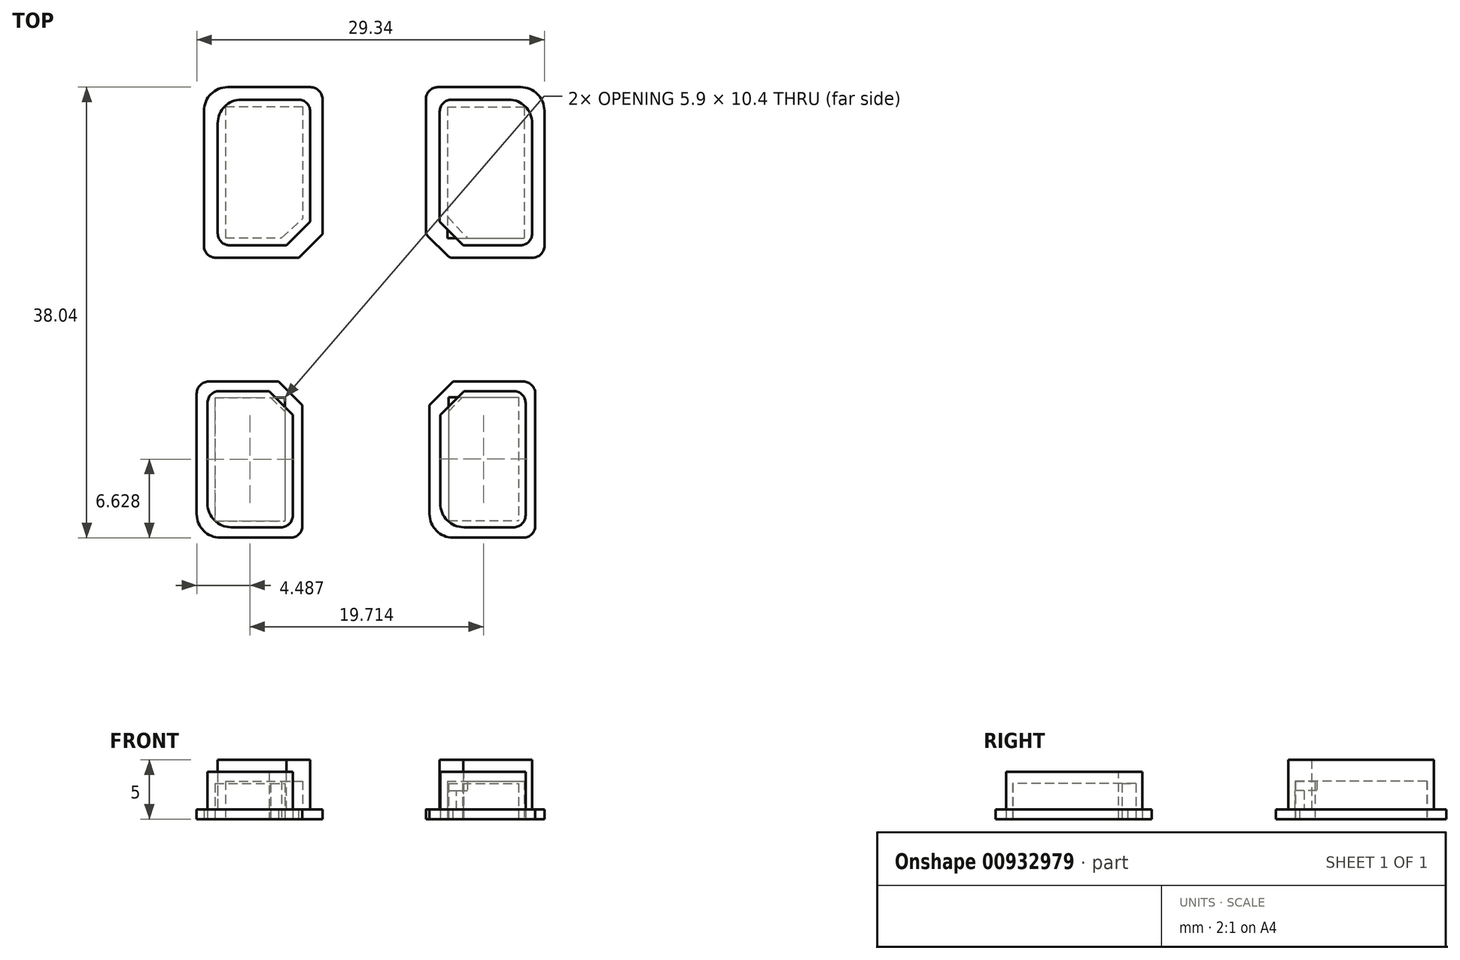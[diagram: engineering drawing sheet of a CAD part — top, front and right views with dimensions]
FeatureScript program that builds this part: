
annotation { "Feature Type Name" : "Feature", "Feature Type Description" : "" }
export const myFeature = defineFeature(function(context is Context, id is Id, definition is map)
    precondition{}
    {
        {
            var Q0;
            Q0=qCreatedBy(makeId("Top.planeOp"),FACE);
            var sketch = newSketch(context, id + "F0", { "sketchPlane" : qUnion([Q0])});
            skLineSegment(sketch, "E0.bottom", {"start": v(-38.74, 12.3) * mm, "end": v(-30.94, 12.3) * mm});
            skLineSegment(sketch, "E0.top", {"start": v(-38.74, 0) * mm, "end": v(-30.94, 0) * mm});
            skLineSegment(sketch, "E0.left", {"start": v(-38.74, 12.3) * mm, "end": v(-38.74, 0) * mm});
            skLineSegment(sketch, "E0.right", {"start": v(-30.94, 12.3) * mm, "end": v(-30.94, 0) * mm});
            skLineSegment(sketch, "E1.bottom", {"start": v(-39.9, 13.35) * mm, "end": v(-29.9, 13.35) * mm});
            skLineSegment(sketch, "E1.top", {"start": v(-39.9, -1.05) * mm, "end": v(-29.9, -1.05) * mm});
            skLineSegment(sketch, "E1.left", {"start": v(-39.9, 13.35) * mm, "end": v(-39.9, -1.05) * mm});
            skLineSegment(sketch, "E1.right", {"start": v(-29.9, 13.35) * mm, "end": v(-29.9, -1.05) * mm});
            skLineSegment(sketch, "E2.bottom", {"start": v(-20, 12.3) * mm, "end": v(-12.2, 12.3) * mm});
            skLineSegment(sketch, "E2.top", {"start": v(-20, 0) * mm, "end": v(-12.2, 0) * mm});
            skLineSegment(sketch, "E2.left", {"start": v(-20, 12.3) * mm, "end": v(-20, 0) * mm});
            skLineSegment(sketch, "E2.right", {"start": v(-12.2, 12.3) * mm, "end": v(-12.2, 0) * mm});
            skLineSegment(sketch, "E3.bottom", {"start": v(-21.17, 13.35) * mm, "end": v(-11.17, 13.35) * mm});
            skLineSegment(sketch, "E3.top", {"start": v(-21.17, -1.05) * mm, "end": v(-11.17, -1.05) * mm});
            skLineSegment(sketch, "E3.left", {"start": v(-21.17, 13.35) * mm, "end": v(-21.17, -1.05) * mm});
            skLineSegment(sketch, "E3.right", {"start": v(-11.17, 13.35) * mm, "end": v(-11.17, -1.05) * mm});
            skLineSegment(sketch, "E4.bottom", {"start": v(-38.08, 11.72) * mm, "end": v(-31.58, 11.72) * mm});
            skLineSegment(sketch, "E4.top", {"start": v(-38.08, 0.62) * mm, "end": v(-31.58, 0.62) * mm});
            skLineSegment(sketch, "E4.left", {"start": v(-38.08, 11.72) * mm, "end": v(-38.08, 0.62) * mm});
            skLineSegment(sketch, "E4.right", {"start": v(-31.58, 11.72) * mm, "end": v(-31.58, 0.62) * mm});
            skLineSegment(sketch, "E5.bottom", {"start": v(-19.36, 11.7) * mm, "end": v(-12.86, 11.7) * mm});
            skLineSegment(sketch, "E5.top", {"start": v(-19.36, 0.6) * mm, "end": v(-12.86, 0.6) * mm});
            skLineSegment(sketch, "E5.left", {"start": v(-19.36, 11.7) * mm, "end": v(-19.36, 0.6) * mm});
            skLineSegment(sketch, "E5.right", {"start": v(-12.86, 11.7) * mm, "end": v(-12.86, 0.6) * mm});
            skLineSegment(sketch, "E6", {"start": v(-33.34, 0.62) * mm, "end": v(-31.58, 2.25) * mm});
            skLineSegment(sketch, "E7", {"start": v(-19.36, 2.44) * mm, "end": v(-17.65, 0.6) * mm});
            skSolve(sketch);
        }
        {
            var Q0;
            Q0=makeQuery(id+"F0.imprint","IMPRINT",FACE,{"disambiguationData":[TD([[makeQuery(id+"F0.imprint","IMPRINT",EDGE,{"derivedFrom":sQuery(id+"F0.wireOp",EDGE,"E0.bottom")}),-1.0]])]});
            var Q1;
            Q1=makeQuery(id+"F0.imprint","IMPRINT",FACE,{"disambiguationData":[TD([[makeQuery(id+"F0.imprint","IMPRINT",EDGE,{"derivedFrom":sQuery(id+"F0.wireOp",EDGE,"E2.bottom")}),-1.0]])]});
            var Q2;
            Q2=makeQuery(id+"F0.imprint","IMPRINT",FACE,{"disambiguationData":[TD([[makeQuery(id+"F0.imprint","IMPRINT",EDGE,{"derivedFrom":sQuery(id+"F0.wireOp",EDGE,"E5.bottom")}),-1.0]])]});
            var Q3;
            Q3=makeQuery(id+"F0.imprint","IMPRINT",FACE,{"disambiguationData":[TD([[makeQuery(id+"F0.imprint","IMPRINT",EDGE,{"derivedFrom":sQuery(id+"F0.wireOp",EDGE,"E4.bottom")}),-1.0]])]});
            var Q4;
            {var subQ0=sQuery(id+"F0.wireOp",EDGE,"E5.left");var subQ1=sQuery(id+"F0.wireOp",EDGE,"E5.top");var subQ2=makeQuery(id+"F0.imprint","INTERSECT",VERTEX,{"derivedFrom":[subQ1,subQ0]});Q4=makeQuery(id+"F0.imprint","IMPRINT",FACE,{"disambiguationData":[TD([[makeQuery(id+"F0.imprint","IMPRINT",EDGE,{"disambiguationData":[TD([[subQ2,-1.0]])],"derivedFrom":subQ1}),1.0]])]});}
            var Q5;
            {var subQ3=sQuery(id+"F0.wireOp",EDGE,"E6");Q5=makeQuery(id+"F0.imprint","IMPRINT",FACE,{"disambiguationData":[TD([[makeQuery(id+"F0.imprint","IMPRINT",EDGE,{"derivedFrom":subQ3}),-1.0]])]});}
            extrude(context, id + "F1", {"entities" : qUnion([Q0, Q1, Q2, Q3, Q4, Q5]), "depth" : 5 * mm, "offsetDistance" : 25 * mm});
        }
        {
            var Q0;
            Q0=makeQuery(id+"F0.imprint","IMPRINT",FACE,{"disambiguationData":[TD([[makeQuery(id+"F0.imprint","IMPRINT",EDGE,{"derivedFrom":sQuery(id+"F0.wireOp",EDGE,"E0.bottom")}),1.0]])]});
            extrude(context, id + "F2", {"entities" : qUnion([Q0]), "operationType" : NewBodyOperationType.ADD, "depth" : .8 * mm, "offsetDistance" : 25 * mm});
        }
        {
            var Q0;
            Q0=makeQuery(id+"F1.opExtrude","SWEPT_EDGE",EDGE,{"disambiguationData":[OSD([sQuery(id+"F0.wireOp",EDGE,"E0.top"),sQuery(id+"F0.wireOp",EDGE,"E0.left")])]});
            var Q1;
            Q1=makeQuery(id+"F2.opExtrude","SWEPT_EDGE",EDGE,{"disambiguationData":[OSD([sQuery(id+"F0.wireOp",EDGE,"E1.top"),sQuery(id+"F0.wireOp",EDGE,"E1.left")])]});
            var Q2;
            Q2=makeQuery(id+"F2.opExtrude","SWEPT_EDGE",EDGE,{"disambiguationData":[OSD([sQuery(id+"F0.wireOp",EDGE,"E1.bottom"),sQuery(id+"F0.wireOp",EDGE,"E1.right")])]});
            var Q3;
            Q3=makeQuery(id+"F1.opExtrude","SWEPT_EDGE",EDGE,{"disambiguationData":[OSD([sQuery(id+"F0.wireOp",EDGE,"E0.bottom"),sQuery(id+"F0.wireOp",EDGE,"E0.right")])]});
            var Q4;
            Q4=makeQuery(id+"F2.opExtrude","SWEPT_EDGE",EDGE,{"disambiguationData":[OSD([sQuery(id+"F0.wireOp",EDGE,"E3.top"),sQuery(id+"F0.wireOp",EDGE,"E3.left")])]});
            var Q5;
            Q5=makeQuery(id+"F1.opExtrude","SWEPT_EDGE",EDGE,{"disambiguationData":[OSD([sQuery(id+"F0.wireOp",EDGE,"E2.top"),sQuery(id+"F0.wireOp",EDGE,"E2.right")])]});
            var Q6;
            Q6=makeQuery(id+"F2.opExtrude","SWEPT_EDGE",EDGE,{"disambiguationData":[OSD([sQuery(id+"F0.wireOp",EDGE,"E3.top"),sQuery(id+"F0.wireOp",EDGE,"E3.right")])]});
            var Q7;
            Q7=makeQuery(id+"F2.opExtrude","SWEPT_EDGE",EDGE,{"disambiguationData":[OSD([sQuery(id+"F0.wireOp",EDGE,"E3.bottom"),sQuery(id+"F0.wireOp",EDGE,"E3.left")])]});
            var Q8;
            Q8=makeQuery(id+"F1.opExtrude","SWEPT_EDGE",EDGE,{"disambiguationData":[OSD([sQuery(id+"F0.wireOp",EDGE,"E2.bottom"),sQuery(id+"F0.wireOp",EDGE,"E2.left")])]});
            fillet(context, id + "F3", {"entities" : qUnion([Q0, Q1, Q2, Q3, Q4, Q5, Q6, Q7, Q8]), "radius" : 1 * mm, "tangentPropagation" : true, "allowEdgeOverflow" : false});
        }
        {
            var Q0;
            Q0=makeQuery(id+"F2.opExtrude","SWEPT_EDGE",EDGE,{"disambiguationData":[OSD([sQuery(id+"F0.wireOp",EDGE,"E1.bottom"),sQuery(id+"F0.wireOp",EDGE,"E1.left")])]});
            var Q1;
            Q1=makeQuery(id+"F1.opExtrude","SWEPT_EDGE",EDGE,{"disambiguationData":[OSD([sQuery(id+"F0.wireOp",EDGE,"E0.bottom"),sQuery(id+"F0.wireOp",EDGE,"E0.left")])]});
            var Q2;
            Q2=makeQuery(id+"F2.opExtrude","SWEPT_EDGE",EDGE,{"disambiguationData":[OSD([sQuery(id+"F0.wireOp",EDGE,"E3.bottom"),sQuery(id+"F0.wireOp",EDGE,"E3.right")])]});
            var Q3;
            Q3=makeQuery(id+"F1.opExtrude","SWEPT_EDGE",EDGE,{"disambiguationData":[OSD([sQuery(id+"F0.wireOp",EDGE,"E2.bottom"),sQuery(id+"F0.wireOp",EDGE,"E2.right")])]});
            fillet(context, id + "F4", {"entities" : qUnion([Q0, Q1, Q2, Q3]), "radius" : 2 * mm, "tangentPropagation" : true, "allowEdgeOverflow" : false});
        }
        {
            var Q0;
            Q0=makeQuery(id+"F0.imprint","IMPRINT",FACE,{"disambiguationData":[TD([[makeQuery(id+"F0.imprint","IMPRINT",EDGE,{"derivedFrom":sQuery(id+"F0.wireOp",EDGE,"E2.bottom")}),1.0]])]});
            var Q1;
            Q1=makeQuery(id+"F0.imprint","IMPRINT",FACE,{"disambiguationData":[TD([[makeQuery(id+"F0.imprint","IMPRINT",EDGE,{"derivedFrom":sQuery(id+"F0.wireOp",EDGE,"E2.bottom")}),-1.0]])]});
            var Q2;
            Q2=makeQuery(id+"F0.imprint","IMPRINT",FACE,{"disambiguationData":[TD([[makeQuery(id+"F0.imprint","IMPRINT",EDGE,{"derivedFrom":sQuery(id+"F0.wireOp",EDGE,"E5.bottom")}),-1.0]])]});
            extrude(context, id + "F5", {"entities" : qUnion([Q0, Q1, Q2]), "operationType" : NewBodyOperationType.ADD, "depth" : .8 * mm, "offsetDistance" : 25 * mm});
        }
        {
            var Q0;
            Q0=makeQuery(id+"F5.opExtrude","SWEPT_EDGE",EDGE,{"disambiguationData":[OSD([sQuery(id+"F0.wireOp",EDGE,"E3.top"),sQuery(id+"F0.wireOp",EDGE,"E3.left")])]});
            var Q1;
            Q1=makeQuery(id+"F1.opExtrude","SWEPT_EDGE",EDGE,{"disambiguationData":[OSD([sQuery(id+"F0.wireOp",EDGE,"E2.top"),sQuery(id+"F0.wireOp",EDGE,"E2.left")])]});
            var Q2;
            Q2=makeQuery(id+"F2.opExtrude","SWEPT_EDGE",EDGE,{"disambiguationData":[OSD([sQuery(id+"F0.wireOp",EDGE,"E1.top"),sQuery(id+"F0.wireOp",EDGE,"E1.right")])]});
            var Q3;
            Q3=makeQuery(id+"F1.opExtrude","SWEPT_EDGE",EDGE,{"disambiguationData":[OSD([sQuery(id+"F0.wireOp",EDGE,"E0.top"),sQuery(id+"F0.wireOp",EDGE,"E0.right")])]});
            chamfer(context, id + "F6", {"entities" : qUnion([Q0, Q1, Q2, Q3]), "width" : 2 * mm, "tangentPropagation" : true});
        }
        {
            var Q0;
            {var subQ0=sQuery(id+"F0.wireOp",EDGE,"E3.left");Q0=makeQuery(id+"F6.opChamfer","BLEND_EDGE",EDGE,{"blendedFrom":[makeQuery(id+"F5.opExtrude","SWEPT_EDGE",EDGE,{"disambiguationData":[OSD([sQuery(id+"F0.wireOp",EDGE,"E3.top"),subQ0])]}),makeQuery(id+"F5.opExtrude","SWEPT_FACE",FACE,{"disambiguationData":[OSD([subQ0])]})],"blendedInto":[makeQuery(id+"F5.opExtrude","SWEPT_FACE",FACE,{"disambiguationData":[OSD([subQ0])]})]});}
            var Q1;
            {var subQ0=sQuery(id+"F0.wireOp",EDGE,"E3.top");Q1=makeQuery(id+"F6.opChamfer","BLEND_EDGE",EDGE,{"blendedFrom":[makeQuery(id+"F5.opExtrude","SWEPT_EDGE",EDGE,{"disambiguationData":[OSD([subQ0,sQuery(id+"F0.wireOp",EDGE,"E3.left")])]}),makeQuery(id+"F5.opExtrude","SWEPT_FACE",FACE,{"disambiguationData":[OSD([subQ0])]})],"blendedInto":[makeQuery(id+"F5.opExtrude","SWEPT_FACE",FACE,{"disambiguationData":[OSD([subQ0])]})]});}
            fillet(context, id + "F7", {"entities" : qUnion([Q0, Q1]), "radius" : .5 * mm, "tangentPropagation" : true, "allowEdgeOverflow" : false});
        }
        {
            var Q0;
            Q0=makeQuery(id+"F5.opExtrude","SWEPT_EDGE",EDGE,{"disambiguationData":[OSD([sQuery(id+"F0.wireOp",EDGE,"E3.bottom"),sQuery(id+"F0.wireOp",EDGE,"E3.right")])]});
            fillet(context, id + "F8", {"entities" : qUnion([Q0]), "radius" : 2 * mm, "tangentPropagation" : true, "allowEdgeOverflow" : false});
        }
        {
            var Q0;
            Q0=makeQuery(id+"F5.opExtrude","SWEPT_EDGE",EDGE,{"disambiguationData":[OSD([sQuery(id+"F0.wireOp",EDGE,"E3.top"),sQuery(id+"F0.wireOp",EDGE,"E3.right")])]});
            var Q1;
            Q1=makeQuery(id+"F5.opExtrude","SWEPT_EDGE",EDGE,{"disambiguationData":[OSD([sQuery(id+"F0.wireOp",EDGE,"E3.bottom"),sQuery(id+"F0.wireOp",EDGE,"E3.left")])]});
            fillet(context, id + "F9", {"entities" : qUnion([Q0, Q1]), "radius" : 1 * mm, "tangentPropagation" : true, "allowEdgeOverflow" : false});
        }
        {
            var Q0;
            Q0=qCreatedBy(makeId("Top.planeOp"),FACE);
            var sketch = newSketch(context, id + "F10", { "sketchPlane" : qUnion([Q0])});
            skLineSegment(sketch, "E8.bottom", {"start": v(-39.6, -12.3) * mm, "end": v(-32.4, -12.3) * mm});
            skLineSegment(sketch, "E8.top", {"start": v(-39.6, -23.8) * mm, "end": v(-32.4, -23.8) * mm});
            skLineSegment(sketch, "E8.left", {"start": v(-39.6, -12.3) * mm, "end": v(-39.6, -23.8) * mm});
            skLineSegment(sketch, "E8.right", {"start": v(-32.4, -12.3) * mm, "end": v(-32.4, -23.8) * mm});
            skLineSegment(sketch, "E9.bottom", {"start": v(-31.6, -24.69) * mm, "end": v(-40.51, -24.69) * mm});
            skLineSegment(sketch, "E9.top", {"start": v(-31.6, -11.5) * mm, "end": v(-40.51, -11.5) * mm});
            skLineSegment(sketch, "E9.left", {"start": v(-31.6, -24.69) * mm, "end": v(-31.6, -11.5) * mm});
            skLineSegment(sketch, "E9.right", {"start": v(-40.51, -24.69) * mm, "end": v(-40.51, -11.5) * mm});
            skLineSegment(sketch, "E10.bottom", {"start": v(-19.96, -12.3) * mm, "end": v(-12.76, -12.3) * mm});
            skLineSegment(sketch, "E10.top", {"start": v(-19.96, -23.8) * mm, "end": v(-12.76, -23.8) * mm});
            skLineSegment(sketch, "E10.left", {"start": v(-19.96, -12.3) * mm, "end": v(-19.96, -23.8) * mm});
            skLineSegment(sketch, "E10.right", {"start": v(-12.76, -12.3) * mm, "end": v(-12.76, -23.8) * mm});
            skLineSegment(sketch, "E11.bottom", {"start": v(-11.95, -24.69) * mm, "end": v(-20.87, -24.69) * mm});
            skLineSegment(sketch, "E11.top", {"start": v(-11.95, -11.5) * mm, "end": v(-20.87, -11.5) * mm});
            skLineSegment(sketch, "E11.left", {"start": v(-11.95, -24.69) * mm, "end": v(-11.95, -11.5) * mm});
            skLineSegment(sketch, "E11.right", {"start": v(-20.87, -24.69) * mm, "end": v(-20.87, -11.5) * mm});
            skLineSegment(sketch, "E12.bottom", {"start": v(-38.97, -12.86) * mm, "end": v(-33.07, -12.86) * mm});
            skLineSegment(sketch, "E12.top", {"start": v(-38.97, -23.26) * mm, "end": v(-33.07, -23.26) * mm});
            skLineSegment(sketch, "E12.left", {"start": v(-38.97, -12.86) * mm, "end": v(-38.97, -23.26) * mm});
            skLineSegment(sketch, "E12.right", {"start": v(-33.07, -12.86) * mm, "end": v(-33.07, -23.26) * mm});
            skLineSegment(sketch, "E13", {"start": v(-34.27, -12.86) * mm, "end": v(-33.07, -14.03) * mm});
            skLineSegment(sketch, "E14.bottom", {"start": v(-19.26, -12.84) * mm, "end": v(-13.36, -12.84) * mm});
            skLineSegment(sketch, "E14.top", {"start": v(-19.26, -23.24) * mm, "end": v(-13.36, -23.24) * mm});
            skLineSegment(sketch, "E14.left", {"start": v(-19.26, -12.84) * mm, "end": v(-19.26, -23.24) * mm});
            skLineSegment(sketch, "E14.right", {"start": v(-13.36, -12.84) * mm, "end": v(-13.36, -23.24) * mm});
            skLineSegment(sketch, "E15", {"start": v(-19.26, -14.03) * mm, "end": v(-18.1, -12.84) * mm});
            skSolve(sketch);
        }
        {
            var Q0;
            Q0=makeQuery(id+"F10.imprint","IMPRINT",FACE,{"disambiguationData":[TD([[makeQuery(id+"F10.imprint","IMPRINT",EDGE,{"derivedFrom":sQuery(id+"F10.wireOp",EDGE,"E8.bottom")}),-1.0]])]});
            var Q1;
            Q1=makeQuery(id+"F10.imprint","IMPRINT",FACE,{"disambiguationData":[TD([[makeQuery(id+"F10.imprint","IMPRINT",EDGE,{"derivedFrom":sQuery(id+"F10.wireOp",EDGE,"E10.bottom")}),-1.0]])]});
            var Q2;
            {var subQ1=sQuery(id+"F10.wireOp",EDGE,"E12.top");Q2=makeQuery(id+"F10.imprint","IMPRINT",FACE,{"disambiguationData":[TD([[makeQuery(id+"F10.imprint","IMPRINT",EDGE,{"derivedFrom":subQ1}),1.0]])]});}
            var Q3;
            {var subQ3=sQuery(id+"F10.wireOp",EDGE,"E13");Q3=makeQuery(id+"F10.imprint","IMPRINT",FACE,{"disambiguationData":[TD([[makeQuery(id+"F10.imprint","IMPRINT",EDGE,{"derivedFrom":subQ3}),1.0]])]});}
            var Q4;
            {var subQ3=sQuery(id+"F10.wireOp",EDGE,"E15");Q4=makeQuery(id+"F10.imprint","IMPRINT",FACE,{"disambiguationData":[TD([[makeQuery(id+"F10.imprint","IMPRINT",EDGE,{"derivedFrom":subQ3}),1.0]])]});}
            var Q5;
            {var subQ2=sQuery(id+"F10.wireOp",EDGE,"E14.top");Q5=makeQuery(id+"F10.imprint","IMPRINT",FACE,{"disambiguationData":[TD([[makeQuery(id+"F10.imprint","IMPRINT",EDGE,{"derivedFrom":subQ2}),1.0]])]});}
            extrude(context, id + "F11", {"entities" : qUnion([Q0, Q1, Q2, Q3, Q4, Q5]), "depth" : 4 * mm, "offsetDistance" : 25 * mm});
        }
        {
            var Q0;
            Q0=makeQuery(id+"F10.imprint","IMPRINT",FACE,{"disambiguationData":[TD([[makeQuery(id+"F10.imprint","IMPRINT",EDGE,{"derivedFrom":sQuery(id+"F10.wireOp",EDGE,"E8.bottom")}),1.0]])]});
            var Q1;
            Q1=makeQuery(id+"F10.imprint","IMPRINT",FACE,{"disambiguationData":[TD([[makeQuery(id+"F10.imprint","IMPRINT",EDGE,{"derivedFrom":sQuery(id+"F10.wireOp",EDGE,"E10.bottom")}),1.0]])]});
            var Q2;
            Q2=makeQuery(id+"F10.imprint","IMPRINT",FACE,{"disambiguationData":[TD([[makeQuery(id+"F10.imprint","IMPRINT",EDGE,{"derivedFrom":sQuery(id+"F10.wireOp",EDGE,"E10.bottom")}),-1.0]])]});
            var Q3;
            Q3=makeQuery(id+"F10.imprint","IMPRINT",FACE,{"disambiguationData":[TD([[makeQuery(id+"F10.imprint","IMPRINT",EDGE,{"derivedFrom":sQuery(id+"F10.wireOp",EDGE,"E8.bottom")}),-1.0]])]});
            extrude(context, id + "F12", {"entities" : qUnion([Q0, Q1, Q2, Q3]), "depth" : .8 * mm, "offsetDistance" : 25 * mm});
        }
        {
            var Q0;
            Q0=makeQuery(id+"F11.opExtrude","SWEPT_EDGE",EDGE,{"disambiguationData":[OSD([sQuery(id+"F10.wireOp",EDGE,"E8.top"),sQuery(id+"F10.wireOp",EDGE,"E8.left")])]});
            var Q1;
            Q1=makeQuery(id+"F12.opExtrude","SWEPT_EDGE",EDGE,{"disambiguationData":[OSD([sQuery(id+"F10.wireOp",EDGE,"E9.bottom"),sQuery(id+"F10.wireOp",EDGE,"E9.right")])]});
            var Q2;
            Q2=makeQuery(id+"F11.opExtrude","SWEPT_EDGE",EDGE,{"disambiguationData":[OSD([sQuery(id+"F10.wireOp",EDGE,"E10.top"),sQuery(id+"F10.wireOp",EDGE,"E10.left")])]});
            var Q3;
            Q3=makeQuery(id+"F12.opExtrude","SWEPT_EDGE",EDGE,{"disambiguationData":[OSD([sQuery(id+"F10.wireOp",EDGE,"E11.bottom"),sQuery(id+"F10.wireOp",EDGE,"E11.right")])]});
            fillet(context, id + "F13", {"entities" : qUnion([Q0, Q1, Q2, Q3]), "radius" : 2 * mm, "tangentPropagation" : true, "allowEdgeOverflow" : false});
        }
        {
            var Q0;
            Q0=makeQuery(id+"F11.opExtrude","SWEPT_EDGE",EDGE,{"disambiguationData":[OSD([sQuery(id+"F10.wireOp",EDGE,"E8.top"),sQuery(id+"F10.wireOp",EDGE,"E8.right")])]});
            var Q1;
            Q1=makeQuery(id+"F12.opExtrude","SWEPT_EDGE",EDGE,{"disambiguationData":[OSD([sQuery(id+"F10.wireOp",EDGE,"E9.bottom"),sQuery(id+"F10.wireOp",EDGE,"E9.left")])]});
            var Q2;
            Q2=makeQuery(id+"F11.opExtrude","SWEPT_EDGE",EDGE,{"disambiguationData":[OSD([sQuery(id+"F10.wireOp",EDGE,"E10.top"),sQuery(id+"F10.wireOp",EDGE,"E10.right")])]});
            var Q3;
            Q3=makeQuery(id+"F12.opExtrude","SWEPT_EDGE",EDGE,{"disambiguationData":[OSD([sQuery(id+"F10.wireOp",EDGE,"E11.bottom"),sQuery(id+"F10.wireOp",EDGE,"E11.left")])]});
            var Q4;
            Q4=makeQuery(id+"F11.opExtrude","SWEPT_EDGE",EDGE,{"disambiguationData":[OSD([sQuery(id+"F10.wireOp",EDGE,"E10.bottom"),sQuery(id+"F10.wireOp",EDGE,"E10.right")])]});
            var Q5;
            Q5=makeQuery(id+"F12.opExtrude","SWEPT_EDGE",EDGE,{"disambiguationData":[OSD([sQuery(id+"F10.wireOp",EDGE,"E11.top"),sQuery(id+"F10.wireOp",EDGE,"E11.left")])]});
            var Q6;
            Q6=makeQuery(id+"F11.opExtrude","SWEPT_EDGE",EDGE,{"disambiguationData":[OSD([sQuery(id+"F10.wireOp",EDGE,"E8.bottom"),sQuery(id+"F10.wireOp",EDGE,"E8.left")])]});
            var Q7;
            Q7=makeQuery(id+"F12.opExtrude","SWEPT_EDGE",EDGE,{"disambiguationData":[OSD([sQuery(id+"F10.wireOp",EDGE,"E9.top"),sQuery(id+"F10.wireOp",EDGE,"E9.right")])]});
            fillet(context, id + "F14", {"entities" : qUnion([Q0, Q1, Q2, Q3, Q4, Q5, Q6, Q7]), "radius" : 1 * mm, "tangentPropagation" : true, "allowEdgeOverflow" : false});
        }
        {
            var Q0;
            Q0=makeQuery(id+"F0.imprint","IMPRINT",FACE,{"disambiguationData":[TD([[makeQuery(id+"F0.imprint","IMPRINT",EDGE,{"derivedFrom":sQuery(id+"F0.wireOp",EDGE,"E4.bottom")}),-1.0]])]});
            var Q1;
            Q1=makeQuery(id+"F0.imprint","IMPRINT",FACE,{"disambiguationData":[TD([[makeQuery(id+"F0.imprint","IMPRINT",EDGE,{"derivedFrom":sQuery(id+"F0.wireOp",EDGE,"E5.bottom")}),-1.0]])]});
            extrude(context, id + "F15", {"entities" : qUnion([Q0, Q1]), "operationType" : NewBodyOperationType.REMOVE, "depth" : 3.2 * mm, "offsetDistance" : 25 * mm});
        }
        {
            var Q0;
            Q0=makeQuery(id+"F0.imprint","IMPRINT",FACE,{"disambiguationData":[TD([[makeQuery(id+"F0.imprint","IMPRINT",EDGE,{"derivedFrom":sQuery(id+"F0.wireOp",EDGE,"E4.bottom")}),-1.0]])]});
            var Q1;
            {var subQ0=sQuery(id+"F0.wireOp",EDGE,"E5.left");var subQ1=sQuery(id+"F0.wireOp",EDGE,"E5.top");var subQ2=makeQuery(id+"F0.imprint","INTERSECT",VERTEX,{"derivedFrom":[subQ1,subQ0]});Q1=makeQuery(id+"F0.imprint","IMPRINT",FACE,{"disambiguationData":[TD([[makeQuery(id+"F0.imprint","IMPRINT",EDGE,{"disambiguationData":[TD([[subQ2,-1.0]])],"derivedFrom":subQ1}),1.0]])]});}
            extrude(context, id + "F16", {"entities" : qUnion([Q0, Q1]), "operationType" : NewBodyOperationType.REMOVE, "depth" : 2.4 * mm, "offsetDistance" : 25 * mm});
        }
        {
            var Q0;
            {var subQ1=sQuery(id+"F10.wireOp",EDGE,"E12.top");Q0=makeQuery(id+"F10.imprint","IMPRINT",FACE,{"disambiguationData":[TD([[makeQuery(id+"F10.imprint","IMPRINT",EDGE,{"derivedFrom":subQ1}),1.0]])]});}
            extrude(context, id + "F17", {"entities" : qUnion([Q0]), "operationType" : NewBodyOperationType.REMOVE, "depth" : 3 * mm, "offsetDistance" : 25 * mm});
        }
        {
            var Q0;
            {var subQ2=sQuery(id+"F10.wireOp",EDGE,"E14.top");Q0=makeQuery(id+"F10.imprint","IMPRINT",FACE,{"disambiguationData":[TD([[makeQuery(id+"F10.imprint","IMPRINT",EDGE,{"derivedFrom":subQ2}),1.0]])]});}
            extrude(context, id + "F18", {"entities" : qUnion([Q0]), "operationType" : NewBodyOperationType.REMOVE, "depth" : 3 * mm, "offsetDistance" : 25 * mm});
        }
        {
            var Q0;
            Q0=makeQuery(id+"F11.opExtrude","SWEPT_EDGE",EDGE,{"disambiguationData":[OSD([sQuery(id+"F10.wireOp",EDGE,"E8.bottom"),sQuery(id+"F10.wireOp",EDGE,"E8.right")])]});
            var Q1;
            Q1=makeQuery(id+"F12.opExtrude","SWEPT_EDGE",EDGE,{"disambiguationData":[OSD([sQuery(id+"F10.wireOp",EDGE,"E9.top"),sQuery(id+"F10.wireOp",EDGE,"E9.left")])]});
            var Q2;
            Q2=makeQuery(id+"F11.opExtrude","SWEPT_EDGE",EDGE,{"disambiguationData":[OSD([sQuery(id+"F10.wireOp",EDGE,"E10.bottom"),sQuery(id+"F10.wireOp",EDGE,"E10.left")])]});
            var Q3;
            Q3=makeQuery(id+"F12.opExtrude","SWEPT_EDGE",EDGE,{"disambiguationData":[OSD([sQuery(id+"F10.wireOp",EDGE,"E11.top"),sQuery(id+"F10.wireOp",EDGE,"E11.right")])]});
            chamfer(context, id + "F19", {"entities" : qUnion([Q0, Q1, Q2, Q3]), "width" : (2) * mm, "tangentPropagation" : true});
        }
    });
